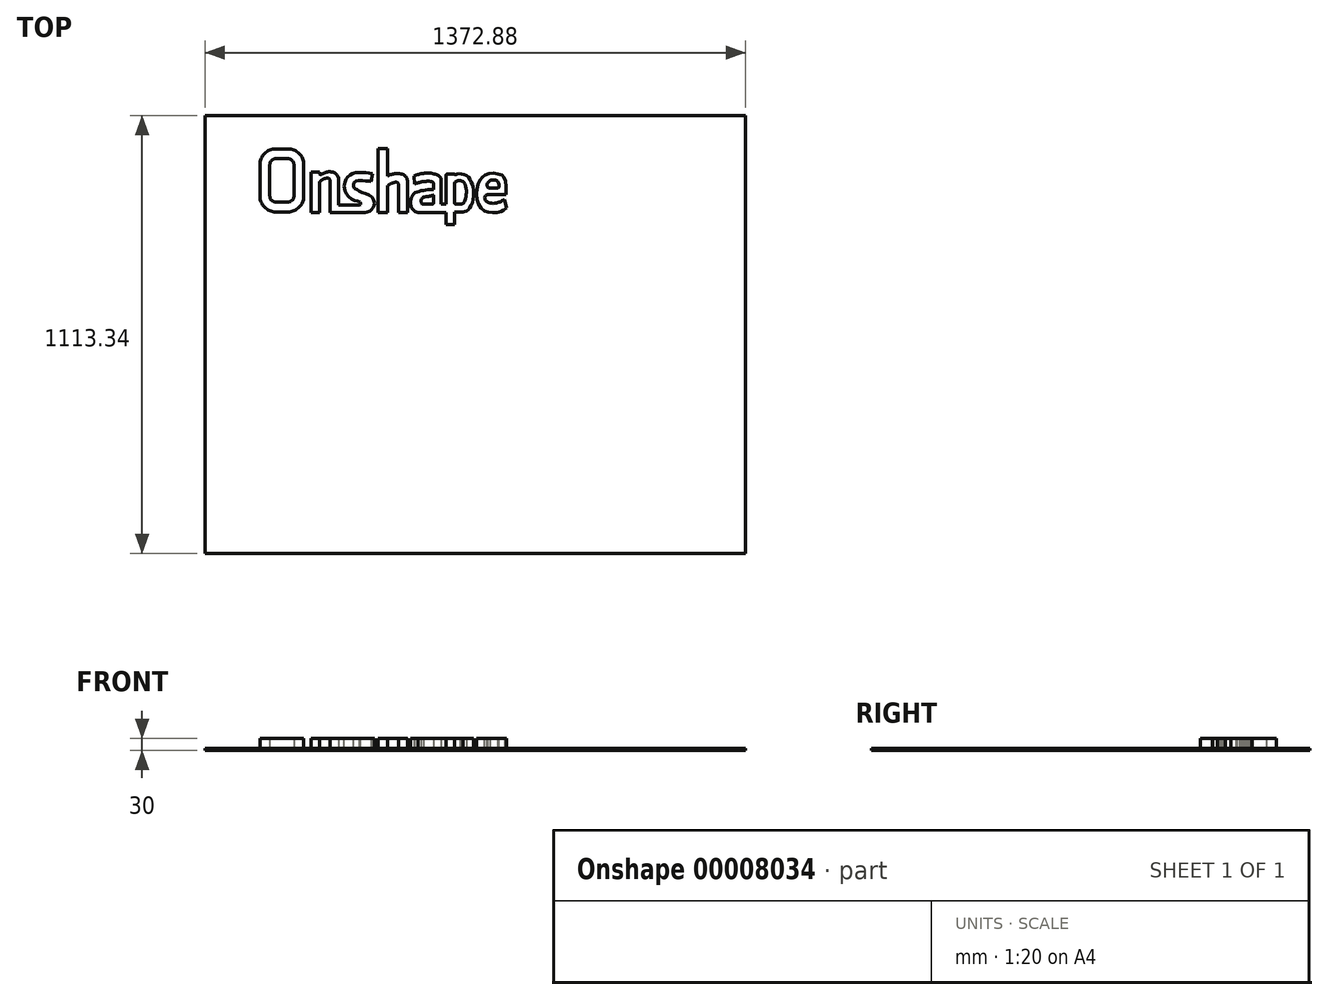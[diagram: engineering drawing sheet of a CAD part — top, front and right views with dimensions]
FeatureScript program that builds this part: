
annotation { "Feature Type Name" : "Feature", "Feature Type Description" : "" }
export const myFeature = defineFeature(function(context is Context, id is Id, definition is map)
    precondition{}
    {
        {
            var Q0;
            Q0=qCreatedBy(makeId("Top.planeOp"),FACE);
            var sketch = newSketch(context, id + "F0", { "sketchPlane" : qUnion([Q0])});
            skLineSegment(sketch, "E0.bottom", {"start": v(-686.44, 556.67) * mm, "end": v(686.44, 556.67) * mm});
            skLineSegment(sketch, "E0.top", {"start": v(-686.44, -556.67) * mm, "end": v(686.44, -556.67) * mm});
            skLineSegment(sketch, "E0.left", {"start": v(-686.44, 556.67) * mm, "end": v(-686.44, -556.67) * mm});
            skLineSegment(sketch, "E0.right", {"start": v(686.44, 556.67) * mm, "end": v(686.44, -556.67) * mm});
            skLineSegment(sketch, "E1", {"start": v(0, 0) * mm, "end": v(285.59, 0) * mm, "construction": true});
            skLineSegment(sketch, "E2", {"start": v(0, 0) * mm, "end": v(0, 273.23) * mm, "construction": true});
            skPoint(sketch, "E3", {"position": v(686.44, 0) * mm});
            skPoint(sketch, "E4", {"position": v(0, 556.67) * mm});
            skSolve(sketch);
        }
        {
            var Q0;
            Q0=makeQuery(id+"F0.imprint","IMPRINT",FACE,{"disambiguationData":[TD([[makeQuery(id+"F0.imprint","IMPRINT",EDGE,{"derivedFrom":sQuery(id+"F0.wireOp",EDGE,"E0.bottom")}),-1.0]])]});
            extrude(context, id + "F1", {"entities" : qUnion([Q0]), "depth" : 5 * mm});
        }
        {
            var Q0;
            Q0=makeQuery(id+"F1.opExtrude","CAP_FACE",FACE,{"disambiguationData":[OSD([sQuery(id+"F0.wireOp",EDGE,"E0.bottom"),sQuery(id+"F0.wireOp",EDGE,"E0.top"),sQuery(id+"F0.wireOp",EDGE,"E0.left"),sQuery(id+"F0.wireOp",EDGE,"E0.right")])],"isStart":false});
            var sketch = newSketch(context, id + "F2", { "sketchPlane" : qUnion([Q0])});
            skLineSegment(sketch, "E5", {"start": v(-546.86, 431.78) * mm, "end": v(-546.86, 351.63) * mm});
            skLineSegment(sketch, "E6", {"start": v(-506.86, 311.63) * mm, "end": v(-475.63, 311.63) * mm});
            skLineSegment(sketch, "E7", {"start": v(-435.63, 351.63) * mm, "end": v(-435.63, 431.78) * mm});
            skLineSegment(sketch, "E8", {"start": v(-475.63, 471.78) * mm, "end": v(-506.86, 471.78) * mm});
            skPoint(sketch, "E9.visualSharp", {"position": v(-546.86, 311.63) * mm});
            skArc(sketch, "E9.filletArc", {"start": v(-546.86, 351.63) * mm, "mid": v(-535.14, 323.35) * mm, "end": v(-506.86, 311.63) * mm});
            skPoint(sketch, "E10.visualSharp", {"position": v(-435.63, 311.63) * mm});
            skArc(sketch, "E10.filletArc", {"start": v(-475.63, 311.63) * mm, "mid": v(-447.34, 323.35) * mm, "end": v(-435.63, 351.63) * mm});
            skPoint(sketch, "E11.visualSharp", {"position": v(-546.86, 471.78) * mm});
            skArc(sketch, "E11.filletArc", {"start": v(-506.86, 471.78) * mm, "mid": v(-535.14, 460.06) * mm, "end": v(-546.86, 431.78) * mm});
            skPoint(sketch, "E12.visualSharp", {"position": v(-435.63, 471.78) * mm});
            skArc(sketch, "E12.filletArc", {"start": v(-435.63, 431.78) * mm, "mid": v(-447.34, 460.06) * mm, "end": v(-475.63, 471.78) * mm});
            skArc(sketch, "E13.0", {"start": v(-506.86, 446.78) * mm, "mid": v(-517.46, 442.38) * mm, "end": v(-521.86, 431.78) * mm});
            skLineSegment(sketch, "E13.1", {"start": v(-475.63, 446.78) * mm, "end": v(-506.86, 446.78) * mm});
            skArc(sketch, "E13.2", {"start": v(-460.63, 431.78) * mm, "mid": v(-465.02, 442.38) * mm, "end": v(-475.63, 446.78) * mm});
            skLineSegment(sketch, "E13.3", {"start": v(-460.63, 351.63) * mm, "end": v(-460.63, 431.78) * mm});
            skArc(sketch, "E13.4", {"start": v(-475.63, 336.63) * mm, "mid": v(-465.02, 341.03) * mm, "end": v(-460.63, 351.63) * mm});
            skLineSegment(sketch, "E13.5", {"start": v(-521.86, 431.78) * mm, "end": v(-521.86, 351.63) * mm});
            skLineSegment(sketch, "E13.6", {"start": v(-506.86, 336.63) * mm, "end": v(-475.63, 336.63) * mm});
            skArc(sketch, "E13.7", {"start": v(-521.86, 351.63) * mm, "mid": v(-517.46, 341.03) * mm, "end": v(-506.86, 336.63) * mm});
            skLineSegment(sketch, "E14", {"start": v(-417.6, 310.1) * mm, "end": v(-417.6, 412.23) * mm});
            skLineSegment(sketch, "E15", {"start": v(-417.6, 412.23) * mm, "end": v(-395.87, 412.23) * mm});
            skLineSegment(sketch, "E16", {"start": v(-395.87, 412.23) * mm, "end": v(-395.87, 409.6) * mm});
            skLineSegment(sketch, "E17", {"start": v(-395.87, 310.1) * mm, "end": v(-417.6, 310.1) * mm});
            skLineSegment(sketch, "E18", {"start": v(-368.55, 390.13) * mm, "end": v(-368.55, 310.1) * mm});
            skLineSegment(sketch, "E19", {"start": v(-368.55, 310.1) * mm, "end": v(-295.29, 310.1) * mm});
            skLineSegment(sketch, "E20", {"start": v(-295.29, 328.96) * mm, "end": v(-347.44, 328.96) * mm});
            skLineSegment(sketch, "E21", {"start": v(-347.44, 328.96) * mm, "end": v(-347.44, 397.9) * mm});
            skFitSpline(sketch, "E22", {"points": [v(-395.87, 387.32) * mm, v(-385.94, 394.77) * mm, v(-372.9, 397.25) * mm, v(-368.55, 391.05) * mm], "startDerivative": vector(24.47, 22.54) * mm, "endDerivative": vector(10.61, -28.3) * mm});
            skFitSpline(sketch, "E23", {"points": [v(-395.87, 408.63) * mm, v(-393.73, 406.28) * mm, v(-391.12, 406.28) * mm, v(-384.6, 409.93) * mm, v(-374.93, 413.33) * mm, v(-361.62, 412.54) * mm, v(-353.53, 407.85) * mm, v(-347.44, 399.3) * mm], "startDerivative": vector(21.71, -30.96) * mm, "endDerivative": vector(33.67, -55.34) * mm});
            skLineSegment(sketch, "E24.trimOffspring", {"start": v(-395.87, 385.12) * mm, "end": v(-395.87, 310.1) * mm});
            skArc(sketch, "E25.filletArc", {"start": v(-347.44, 397.9) * mm, "mid": v(-347.63, 399.26) * mm, "end": v(-348.18, 400.52) * mm});
            skArc(sketch, "E26.filletArc", {"start": v(-368.55, 390.13) * mm, "mid": v(-368.64, 391.05) * mm, "end": v(-368.89, 391.93) * mm});
            skArc(sketch, "E27.filletArc", {"start": v(-394.22, 388.83) * mm, "mid": v(-395.44, 387.15) * mm, "end": v(-395.87, 385.12) * mm});
            skArc(sketch, "E28.filletArc", {"start": v(-395.87, 409.6) * mm, "mid": v(-395.72, 408.64) * mm, "end": v(-395.27, 407.8) * mm});
            skFitSpline(sketch, "E29", {"points": [v(-295.29, 328.96) * mm, v(-292.05, 329.95) * mm, v(-290.85, 331.9) * mm, v(-292.74, 336.46) * mm, v(-304.79, 340.51) * mm, v(-322.88, 351.7) * mm, v(-331.49, 368.73) * mm, v(-332.62, 378.25) * mm, v(-331.32, 386.02) * mm, v(-325.36, 398.7) * mm, v(-313.45, 408.55) * mm, v(-295.29, 411.92) * mm, v(-273.04, 411.14) * mm, v(-265.01, 409.58) * mm], "startDerivative": vector(84.75, 14.56) * mm, "endDerivative": vector(103.74, -25.5) * mm});
            skLineSegment(sketch, "E30", {"start": v(-295.29, 310.1) * mm, "end": v(-279.88, 310.1) * mm});
            skFitSpline(sketch, "E31", {"points": [v(-279.88, 310.1) * mm, v(-268.3, 312.93) * mm, v(-259.93, 321.25) * mm, v(-256.27, 332.24) * mm, v(-262.13, 348.72) * mm, v(-285.2, 360.44) * mm, v(-301.32, 368.13) * mm, v(-309.02, 374.73) * mm, v(-308.65, 384.25) * mm, v(-301.32, 390.85) * mm, v(-279.88, 390.48) * mm, v(-264.33, 389.01) * mm], "startDerivative": vector(97.21, 0) * mm, "endDerivative": vector(103.18, -17.03) * mm});
            skLineSegment(sketch, "E32", {"start": v(-264.33, 389.01) * mm, "end": v(-261.08, 408.71) * mm});
            skLineSegment(sketch, "E33", {"start": v(-261.08, 408.71) * mm, "end": v(-265.01, 409.58) * mm});
            skLineSegment(sketch, "E34", {"start": v(-247.27, 310.1) * mm, "end": v(-247.27, 472.02) * mm});
            skLineSegment(sketch, "E35", {"start": v(-247.27, 472.02) * mm, "end": v(-222.54, 472.02) * mm});
            skLineSegment(sketch, "E36", {"start": v(-222.54, 472.02) * mm, "end": v(-222.54, 402.9) * mm});
            skLineSegment(sketch, "E37", {"start": v(-222.54, 310.1) * mm, "end": v(-247.27, 310.1) * mm});
            skLineSegment(sketch, "E38", {"start": v(-194.85, 310.1) * mm, "end": v(-194.85, 382.16) * mm});
            skLineSegment(sketch, "E39", {"start": v(-172.25, 384.93) * mm, "end": v(-172.25, 310.1) * mm});
            skLineSegment(sketch, "E40", {"start": v(-172.25, 310.1) * mm, "end": v(-194.85, 310.1) * mm});
            skFitSpline(sketch, "E41", {"points": [v(-222.54, 378) * mm, v(-219.3, 380.68) * mm, v(-212.2, 384.35) * mm, v(-203.9, 386.8) * mm, v(-198.02, 386.55) * mm, v(-195.34, 383.3) * mm, v(-194.85, 380.93) * mm], "startDerivative": vector(19.33, 17.96) * mm, "endDerivative": vector(0, -32.88) * mm});
            skFitSpline(sketch, "E42", {"points": [v(-222.54, 402.9) * mm, v(-218.06, 405.15) * mm, v(-211.14, 407.4) * mm, v(-204.57, 408.95) * mm, v(-194.03, 408.95) * mm, v(-184.7, 407.05) * mm, v(-176.92, 402.2) * mm, v(-172.94, 394.6) * mm, v(-172.25, 387.86) * mm, v(-172.25, 384.93) * mm], "startDerivative": vector(44.62, 25.05) * mm, "endDerivative": vector(-0.44, -37.07) * mm});
            skLineSegment(sketch, "E43.trimOffspring", {"start": v(-222.54, 378) * mm, "end": v(-222.54, 310.1) * mm});
            skFitSpline(sketch, "E44", {"points": [v(-155.69, 402.36) * mm, v(-146.29, 406.3) * mm, v(-137.36, 408.56) * mm, v(-125.69, 410.31) * mm, v(-109.55, 409.3) * mm, v(-98.2, 405.93) * mm, v(-90.64, 401.36) * mm, v(-86.45, 394.88) * mm], "startDerivative": vector(46.04, 27.08) * mm, "endDerivative": vector(2.85, -63.73) * mm});
            skLineSegment(sketch, "E45", {"start": v(-86.45, 394.88) * mm, "end": v(-86.45, 331.29) * mm});
            skLineSegment(sketch, "E46", {"start": v(-145.35, 310.1) * mm, "end": v(-73.7, 310.1) * mm});
            skFitSpline(sketch, "E47", {"points": [v(-145.35, 310.1) * mm, v(-152.18, 312.44) * mm, v(-157.9, 317.24) * mm, v(-163.12, 325.3) * mm, v(-164.18, 338.84) * mm, v(-162.7, 346.6) * mm, v(-157.3, 356.7) * mm, v(-146.8, 362.57) * mm, v(-132.2, 366.32) * mm, v(-117.08, 367.97) * mm, v(-105.47, 368.73) * mm], "startDerivative": vector(-83.06, 22.5) * mm, "endDerivative": vector(90.2, 15.78) * mm});
            skLineSegment(sketch, "E48", {"start": v(-105.47, 368.73) * mm, "end": v(-105.47, 381.7) * mm});
            skLineSegment(sketch, "E49", {"start": v(-155.69, 402.36) * mm, "end": v(-154.02, 382.77) * mm});
            skFitSpline(sketch, "E50", {"points": [v(-154.02, 382.77) * mm, v(-144.61, 385.73) * mm, v(-136.68, 387.76) * mm, v(-127.98, 389.02) * mm, v(-120.42, 389.61) * mm, v(-113.87, 389.11) * mm, v(-108.78, 387.18) * mm, v(-105.47, 381.7) * mm], "startDerivative": vector(58.12, 18.51) * mm, "endDerivative": vector(-2.77, -59.3) * mm});
            skLineSegment(sketch, "E51", {"start": v(-105.47, 353.65) * mm, "end": v(-105.47, 336.09) * mm});
            skLineSegment(sketch, "E52", {"start": v(-130.8, 331.09) * mm, "end": v(-110.47, 331.09) * mm});
            skFitSpline(sketch, "E53", {"points": [v(-130.8, 331.09) * mm, v(-134.75, 332.12) * mm, v(-136.48, 334.09) * mm, v(-137.47, 338.28) * mm, v(-136.48, 343.8) * mm, v(-132.78, 348.23) * mm, v(-124.06, 350.62) * mm, v(-114.28, 351.69) * mm, v(-110.25, 352.84) * mm, v(-107.99, 353.65) * mm, v(-106.71, 354.4) * mm, v(-105.85, 354.11) * mm, v(-105.47, 353.65) * mm], "startDerivative": vector(-49.56, 8.3) * mm, "endDerivative": vector(5.14, -15.4) * mm});
            skArc(sketch, "E54.filletArc", {"start": v(-110.47, 331.09) * mm, "mid": v(-106.94, 332.55) * mm, "end": v(-105.47, 336.09) * mm});
            skLineSegment(sketch, "E55", {"start": v(-86.45, 331.29) * mm, "end": v(-73.7, 331.29) * mm});
            skLineSegment(sketch, "E56", {"start": v(-73.7, 331.29) * mm, "end": v(-73.7, 405.67) * mm});
            skLineSegment(sketch, "E57", {"start": v(-73.7, 310.1) * mm, "end": v(-73.7, 279.1) * mm});
            skLineSegment(sketch, "E58", {"start": v(-73.7, 279.1) * mm, "end": v(-52.5, 279.1) * mm});
            skLineSegment(sketch, "E59", {"start": v(-52.5, 279.1) * mm, "end": v(-52.5, 311) * mm});
            skLineSegment(sketch, "E60", {"start": v(-52.5, 311) * mm, "end": v(-31.56, 311) * mm});
            skLineSegment(sketch, "E61", {"start": v(-52.5, 334.29) * mm, "end": v(-52.5, 385.08) * mm});
            skLineSegment(sketch, "E62", {"start": v(-71.7, 407.67) * mm, "end": v(-52.5, 407.67) * mm});
            skArc(sketch, "E63.filletArc", {"start": v(-71.7, 407.67) * mm, "mid": v(-73.12, 407.09) * mm, "end": v(-73.7, 405.67) * mm});
            skLineSegment(sketch, "E64", {"start": v(-49.5, 331.29) * mm, "end": v(-38.01, 331.29) * mm});
            skPoint(sketch, "E65.newPointA", {"position": v(-52.5, 331.29) * mm});
            skArc(sketch, "E65.filletArc", {"start": v(-52.5, 334.29) * mm, "mid": v(-51.62, 332.17) * mm, "end": v(-49.5, 331.29) * mm});
            skFitSpline(sketch, "E66", {"points": [v(-52.5, 385.08) * mm, v(-49.94, 388.2) * mm, v(-47.38, 389.83) * mm, v(-43.9, 391.23) * mm, v(-38.77, 391.46) * mm, v(-32.5, 389.37) * mm, v(-26.91, 383.09) * mm, v(-22.96, 368.9) * mm, v(-22.96, 354.02) * mm, v(-24.82, 343.32) * mm, v(-29.24, 334.94) * mm, v(-33.66, 332.15) * mm, v(-38.01, 331.29) * mm], "startDerivative": vector(39.46, 54.88) * mm, "endDerivative": vector(-66.44, -9.1) * mm});
            skFitSpline(sketch, "E67", {"points": [v(-52.5, 407.67) * mm, v(-52.5, 406.79) * mm, v(-51.95, 406) * mm, v(-49.85, 406.37) * mm, v(-47.08, 407.67) * mm, v(-42.4, 408.34) * mm, v(-31.43, 407.67) * mm, v(-20.88, 402.7) * mm, v(-14.3, 395.36) * mm, v(-8.1, 383.03) * mm, v(-4.79, 370.91) * mm, v(-3.97, 354.44) * mm, v(-6.97, 335.74) * mm, v(-13.61, 322.35) * mm, v(-20.42, 315.24) * mm, v(-25.52, 312.77) * mm, v(-31.56, 311) * mm], "startDerivative": vector(-4.32, -40.56) * mm, "endDerivative": vector(-113.2, -25.5) * mm});
            skPoint(sketch, "E68.orphan", {"position": v(-86.45, 395.44) * mm});
            skFitSpline(sketch, "E69", {"points": [v(79.8, 321.72) * mm, v(72.86, 316.47) * mm, v(68.09, 313.95) * mm, v(61.94, 311.74) * mm, v(52.56, 310) * mm, v(38.01, 309.82) * mm, v(29.22, 311.62) * mm, v(21.33, 315.8) * mm, v(12.16, 323.85) * mm, v(6.23, 336.9) * mm, v(3.46, 351.75) * mm, v(3.78, 368.7) * mm, v(7.04, 382.57) * mm, v(12.79, 393.95) * mm, v(18.22, 399.99) * mm, v(23.27, 404.6) * mm, v(31.61, 408.55) * mm, v(43.68, 410.09) * mm, v(56.42, 408.77) * mm, v(66.3, 405.7) * mm, v(71.56, 401.74) * mm, v(75.51, 394.5) * mm, v(77.49, 386.38) * mm, v(77.7, 356.3) * mm], "startDerivative": vector(-94.33, -93.91) * mm, "endDerivative": vector(-10.07, -512.06) * mm});
            skLineSegment(sketch, "E70", {"start": v(77.7, 356.3) * mm, "end": v(30.73, 356.3) * mm});
            skFitSpline(sketch, "E71", {"points": [v(30.73, 356.3) * mm, v(26.12, 352.57) * mm, v(24.16, 347.8) * mm, v(24.56, 344.05) * mm, v(26.23, 340.56) * mm, v(29.2, 337.79) * mm, v(34.2, 335.06) * mm, v(43.39, 333.35) * mm, v(55.3, 334.72) * mm, v(61.2, 336.58) * mm, v(68.12, 339.58) * mm, v(74.13, 342.72) * mm], "startDerivative": vector(-38.92, -19.1) * mm, "endDerivative": vector(57.68, 31.07) * mm});
            skLineSegment(sketch, "E72", {"start": v(74.13, 342.72) * mm, "end": v(79.8, 321.72) * mm});
            skLineSegment(sketch, "E73", {"start": v(37.23, 371.87) * mm, "end": v(56.14, 371.87) * mm});
            skFitSpline(sketch, "E74", {"points": [v(56.14, 371.87) * mm, v(58.04, 372.46) * mm, v(59.7, 374.29) * mm, v(60, 377.9) * mm, v(59.65, 382.65) * mm, v(57.56, 388.11) * mm, v(53.95, 391.6) * mm, v(47.9, 392.88) * mm, v(40.58, 392.18) * mm, v(35.58, 389.16) * mm, v(32.45, 386.12) * mm, v(30.54, 381.4) * mm, v(30.86, 376.06) * mm, v(33.07, 373.46) * mm, v(37.23, 371.87) * mm], "startDerivative": vector(39.67, 11.95) * mm, "endDerivative": vector(102.32, -7.72) * mm});
            skSolve(sketch);
        }
        {
            var Q0;
            {Q0=qUnion([makeQuery(id+"F2.imprint","IMPRINT",FACE,{"disambiguationData":[TD([[makeQuery(id+"F2.imprint","IMPRINT",EDGE,{"derivedFrom":sQuery(id+"F2.wireOp",EDGE,"E14")}),-1.0]])]}),makeQuery(id+"F2.imprint","IMPRINT",FACE,{"disambiguationData":[TD([[makeQuery(id+"F2.imprint","IMPRINT",EDGE,{"derivedFrom":sQuery(id+"F2.wireOp",EDGE,"E34")}),-1.0]])]}),makeQuery(id+"F2.imprint","IMPRINT",FACE,{"disambiguationData":[TD([[makeQuery(id+"F2.imprint","IMPRINT",EDGE,{"derivedFrom":sQuery(id+"F2.wireOp",EDGE,"E5")}),1.0]])]}),makeQuery(id+"F2.imprint","IMPRINT",FACE,{"disambiguationData":[TD([[makeQuery(id+"F2.imprint","IMPRINT",EDGE,{"derivedFrom":sQuery(id+"F2.wireOp",EDGE,"E69")}),-1.0]])]}),makeQuery(id+"F2.imprint","IMPRINT",FACE,{"disambiguationData":[TD([[makeQuery(id+"F2.imprint","IMPRINT",EDGE,{"derivedFrom":sQuery(id+"F2.wireOp",EDGE,"E44")}),-1.0]])]})]);}
            extrude(context, id + "F3", {"entities" : qUnion([Q0]), "operationType" : NewBodyOperationType.ADD, "depth" : 25 * mm});
        }
    });
